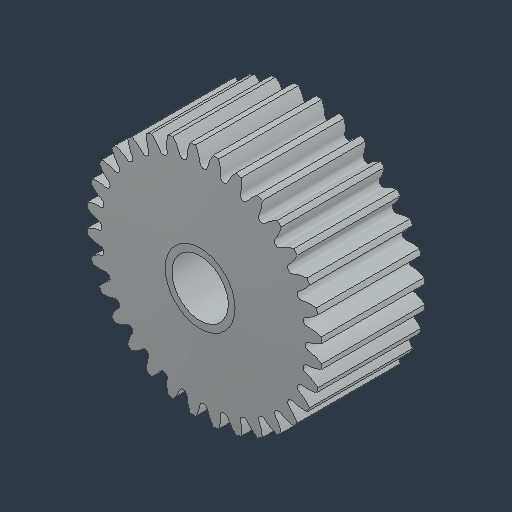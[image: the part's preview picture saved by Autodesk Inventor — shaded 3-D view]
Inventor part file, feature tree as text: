
AUTODESK INVENTOR PART (.ipt)
format: ipt  version: 2024.3 (Build 283343000, 343)  size: 444,416 bytes
history: native  units: in
note: dims shown in document units (in); Inventor stores cm internally (conversion verified against a paired STEP export)
features: mirror x1
ambient origin geometry x8: Origin, YZ Plane, XZ Plane, XY Plane, X Axis, Y Axis, Z Axis, Center Point
bodies: Solid1 (feature_tree)
feature tree (1):
  mirror  "Mirror1"
